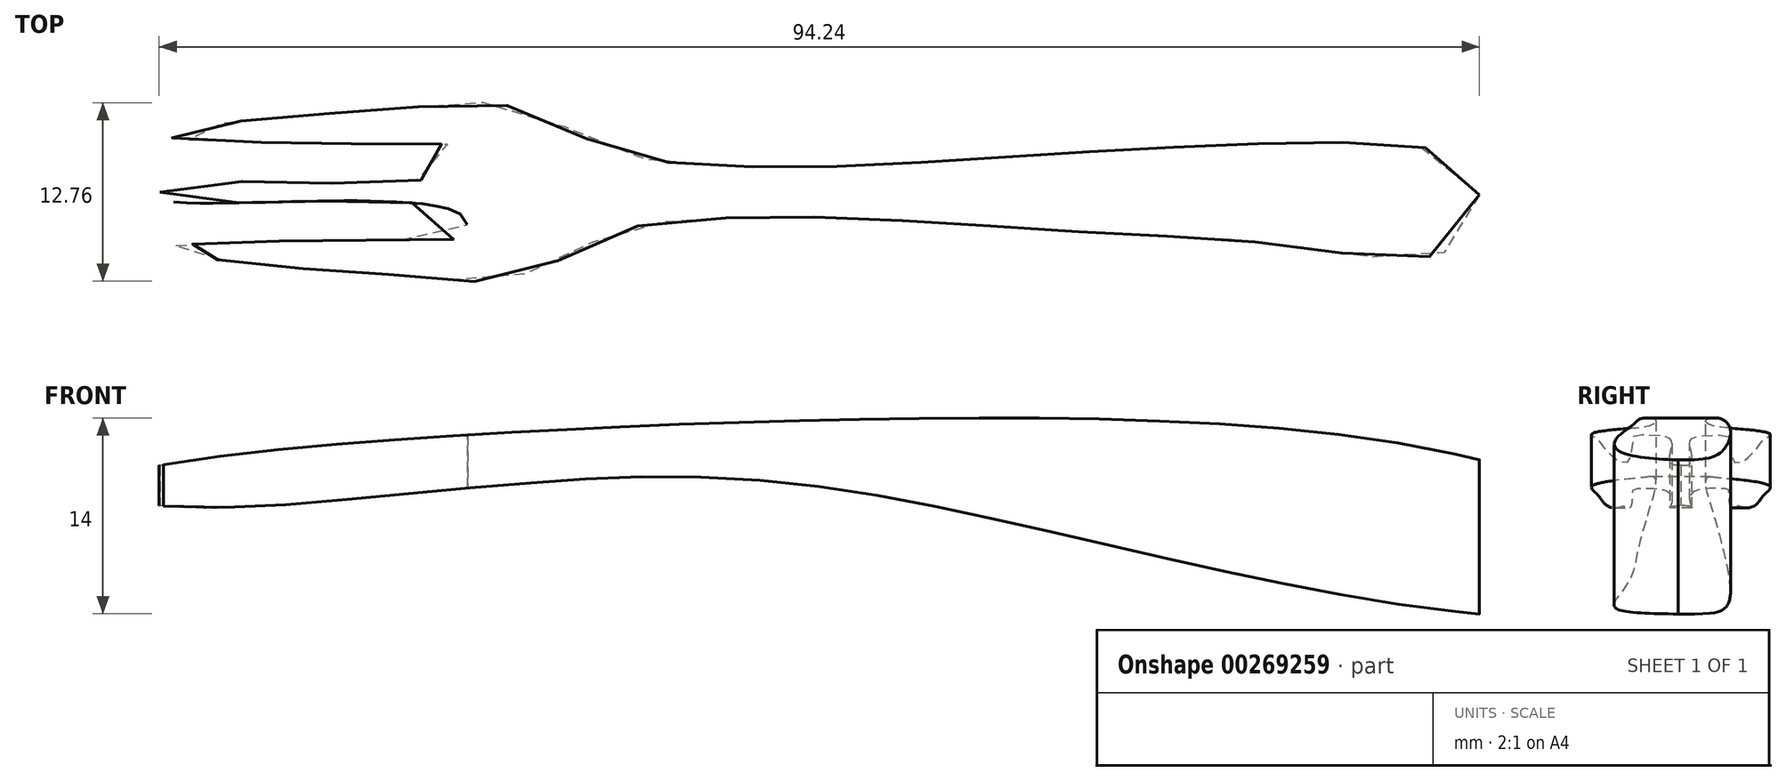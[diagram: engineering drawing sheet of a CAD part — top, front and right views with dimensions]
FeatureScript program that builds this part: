
annotation { "Feature Type Name" : "Feature", "Feature Type Description" : "" }
export const myFeature = defineFeature(function(context is Context, id is Id, definition is map)
    precondition{}
    {
        {
            var Q0;
            Q0=qCreatedBy(makeId("Top.planeOp"),FACE);
            var sketch = newSketch(context, id + "F0", { "sketchPlane" : qUnion([Q0])});
            skPoint(sketch, "E0.endSnap0", {"position": v(-0.07, 45.8) * mm});
            skFitSpline(sketch, "E1", {"points": [v(-48.4, 37.58) * mm, v(-48.23, 37.04) * mm, v(-27.36, 36.21) * mm, v(-26.54, 34.63) * mm, v(-28.89, 34.16) * mm, v(-48.1, 33.57) * mm, v(-43.52, 32.63) * mm, v(-37.24, 32.04) * mm, v(-30.65, 31.57) * mm, v(-23.3, 31.45) * mm, v(-17.54, 33.98) * mm, v(-14.02, 35.21) * mm, v(-2.9, 35.8) * mm, v(7.97, 35.33) * mm, v(21.25, 34.5) * mm, v(27.36, 34.21) * mm, v(33.89, 33.5) * mm, v(43.35, 33.27) * mm, v(45.58, 35.98) * mm, v(45.76, 37.95) * mm], "startDerivative": vector(-12.6, -39.12) * mm, "endDerivative": vector(-1.18, 64.37) * mm});
            skFitSpline(sketch, "E2.MirrorCS", {"points": [v(-48.4, 37.58) * mm, v(-48.23, 38.12) * mm, v(-27.36, 38.94) * mm, v(-26.54, 40.53) * mm, v(-28.89, 41) * mm, v(-48.1, 41.59) * mm, v(-43.52, 42.53) * mm, v(-37.24, 43.11) * mm, v(-30.65, 43.58) * mm, v(-23.3, 43.7) * mm, v(-17.54, 41.17) * mm, v(-14.02, 39.94) * mm, v(-2.9, 39.35) * mm, v(7.97, 39.82) * mm, v(21.25, 40.64) * mm, v(27.36, 40.94) * mm, v(35.42, 41.12) * mm, v(43.53, 40.43) * mm, v(45.58, 39.18) * mm, v(45.76, 37.2) * mm], "startDerivative": vector(-12.6, 39.12) * mm, "endDerivative": vector(-1.18, -64.37) * mm});
            skSolve(sketch);
        }
        {
            var Q0;
            Q0 = qSketchRegion(id + "F0", true);
            extrude(context, id + "F1", {"entities" : qUnion([Q0]), "depth" : 106 * mm});
        }
        {
            var Q0;
            Q0=qCreatedBy(makeId("Front.planeOp"),FACE);
            var sketch = newSketch(context, id + "F2", { "sketchPlane" : qUnion([Q0])});
            skFitSpline(sketch, "E3", {"points": [v(51.14, 18.21) * mm, v(1.94, 22.83) * mm, v(-52.51, 18.21) * mm, v(-48.21, 16.62) * mm, v(-14.46, 18.69) * mm, v(15.48, 14.7) * mm, v(52.42, 8.82) * mm, v(58.95, 12) * mm, v(51.14, 18.21) * mm]});
            skSolve(sketch);
        }
        {
            var Q0;
            Q0=makeQuery(id+"F2.imprint","IMPRINT",FACE,{"disambiguationData":[TD([[makeQuery(id+"F2.imprint","IMPRINT",EDGE,{"derivedFrom":sQuery(id+"F2.wireOp",EDGE,"E3")}),1.0]])]});
            extrude(context, id + "F3", {"entities" : qUnion([Q0]), "operationType" : NewBodyOperationType.INTERSECT, "oppositeDirection" : true, "depth" : 87.4 * mm});
        }
    });
